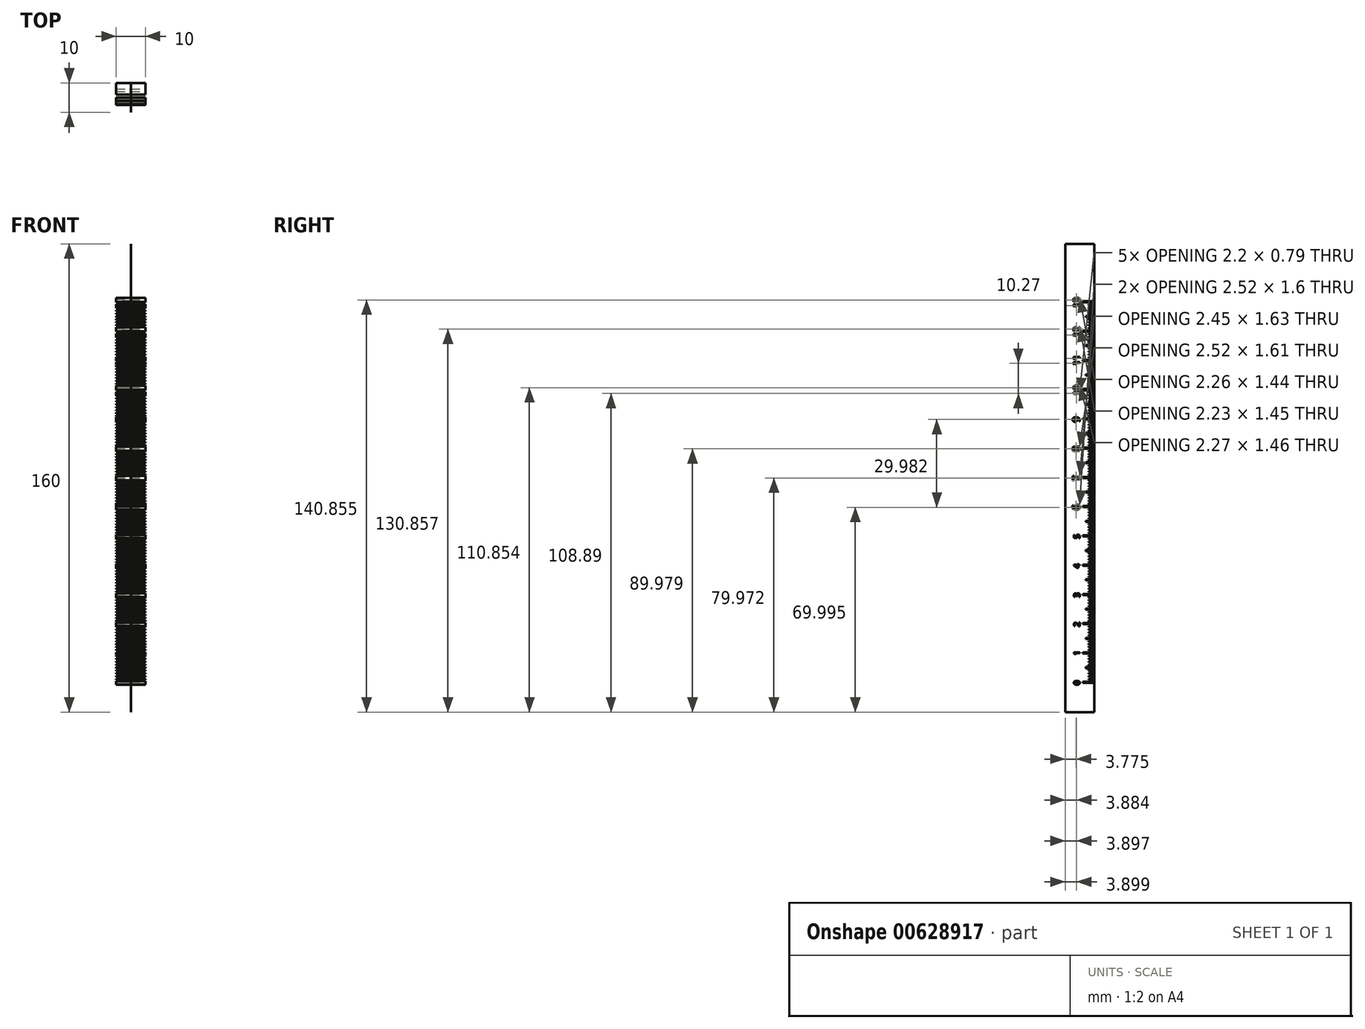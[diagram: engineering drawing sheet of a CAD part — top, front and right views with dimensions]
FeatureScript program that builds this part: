
annotation { "Feature Type Name" : "Feature", "Feature Type Description" : "" }
export const myFeature = defineFeature(function(context is Context, id is Id, definition is map)
    precondition{}
    {
        {
            var Q0;
            Q0=qCreatedBy(makeId("Right.planeOp"),FACE);
            var sketch = newSketch(context, id + "F0", { "sketchPlane" : qUnion([Q0])});
            skLineSegment(sketch, "E0.bottom", {"start": v(-20, 0) * mm, "end": v(-10, 0) * mm});
            skLineSegment(sketch, "E0.top", {"start": v(-20, 160) * mm, "end": v(-10, 160) * mm});
            skLineSegment(sketch, "E0.left", {"start": v(-20, 0) * mm, "end": v(-20, 160) * mm});
            skLineSegment(sketch, "E0.right", {"start": v(-10, 0) * mm, "end": v(-10, 160) * mm});
            skSolve(sketch);
        }
        {
            var Q0;
            Q0=qSketchRegion(id+"F0",true);
            extrude(context, id + "F1", {"entities" : qUnion([Q0]), "depth" : 0.1 * mm, "offsetDistance" : 25 * mm});
        }
        {
            var Q0;
            Q0=qCreatedBy(makeId("Right.planeOp"),FACE);
            var sketch = newSketch(context, id + "F2", { "sketchPlane" : qUnion([Q0])});
            skLineSegment(sketch, "E1", {"start": v(-12, 0) * mm, "end": v(-12, 150) * mm, "construction": true});
            skLineSegment(sketch, "E2", {"start": v(-14, 0) * mm, "end": v(-14, 150) * mm, "construction": true});
            skLineSegment(sketch, "E3", {"start": v(-13, 0) * mm, "end": v(-13, 150) * mm, "construction": true});
            skLineSegment(sketch, "E4.bottom", {"start": v(-14, 10.4) * mm, "end": v(-10, 10.4) * mm});
            skLineSegment(sketch, "E4.top", {"start": v(-14, 10) * mm, "end": v(-10, 10) * mm});
            skLineSegment(sketch, "E4.left", {"start": v(-14, 10) * mm, "end": v(-14, 10.4) * mm});
            skLineSegment(sketch, "E4.right", {"start": v(-10, 10) * mm, "end": v(-10, 10.4) * mm});
            skLineSegment(sketch, "E5.0.1.0", {"start": v(-14, 20.4) * mm, "end": v(-10, 20.4) * mm});
            skLineSegment(sketch, "E5.0.1.1", {"start": v(-14, 20) * mm, "end": v(-10, 20) * mm});
            skLineSegment(sketch, "E5.0.1.2", {"start": v(-14, 20) * mm, "end": v(-14, 20.4) * mm});
            skLineSegment(sketch, "E5.0.1.3", {"start": v(-10, 20) * mm, "end": v(-10, 20.4) * mm});
            skLineSegment(sketch, "E5.0.2.0", {"start": v(-14, 30.4) * mm, "end": v(-10, 30.4) * mm});
            skLineSegment(sketch, "E5.0.2.1", {"start": v(-14, 30) * mm, "end": v(-10, 30) * mm});
            skLineSegment(sketch, "E5.0.2.2", {"start": v(-14, 30) * mm, "end": v(-14, 30.4) * mm});
            skLineSegment(sketch, "E5.0.2.3", {"start": v(-10, 30) * mm, "end": v(-10, 30.4) * mm});
            skLineSegment(sketch, "E5.0.3.0", {"start": v(-14, 40.4) * mm, "end": v(-10, 40.4) * mm});
            skLineSegment(sketch, "E5.0.3.1", {"start": v(-14, 40) * mm, "end": v(-10, 40) * mm});
            skLineSegment(sketch, "E5.0.3.2", {"start": v(-14, 40) * mm, "end": v(-14, 40.4) * mm});
            skLineSegment(sketch, "E5.0.3.3", {"start": v(-10, 40) * mm, "end": v(-10, 40.4) * mm});
            skLineSegment(sketch, "E5.0.4.0", {"start": v(-14, 50.4) * mm, "end": v(-10, 50.4) * mm});
            skLineSegment(sketch, "E5.0.4.1", {"start": v(-14, 50) * mm, "end": v(-10, 50) * mm});
            skLineSegment(sketch, "E5.0.4.2", {"start": v(-14, 50) * mm, "end": v(-14, 50.4) * mm});
            skLineSegment(sketch, "E5.0.4.3", {"start": v(-10, 50) * mm, "end": v(-10, 50.4) * mm});
            skLineSegment(sketch, "E5.0.5.0", {"start": v(-14, 60.4) * mm, "end": v(-10, 60.4) * mm});
            skLineSegment(sketch, "E5.0.5.1", {"start": v(-14, 60) * mm, "end": v(-10, 60) * mm});
            skLineSegment(sketch, "E5.0.5.2", {"start": v(-14, 60) * mm, "end": v(-14, 60.4) * mm});
            skLineSegment(sketch, "E5.0.5.3", {"start": v(-10, 60) * mm, "end": v(-10, 60.4) * mm});
            skLineSegment(sketch, "E5.0.6.0", {"start": v(-14, 70.4) * mm, "end": v(-10, 70.4) * mm});
            skLineSegment(sketch, "E5.0.6.1", {"start": v(-14, 70) * mm, "end": v(-10, 70) * mm});
            skLineSegment(sketch, "E5.0.6.2", {"start": v(-14, 70) * mm, "end": v(-14, 70.4) * mm});
            skLineSegment(sketch, "E5.0.6.3", {"start": v(-10, 70) * mm, "end": v(-10, 70.4) * mm});
            skLineSegment(sketch, "E5.0.7.0", {"start": v(-14, 80.4) * mm, "end": v(-10, 80.4) * mm});
            skLineSegment(sketch, "E5.0.7.1", {"start": v(-14, 80) * mm, "end": v(-10, 80) * mm});
            skLineSegment(sketch, "E5.0.7.2", {"start": v(-14, 80) * mm, "end": v(-14, 80.4) * mm});
            skLineSegment(sketch, "E5.0.7.3", {"start": v(-10, 80) * mm, "end": v(-10, 80.4) * mm});
            skLineSegment(sketch, "E5.0.8.0", {"start": v(-14, 90.4) * mm, "end": v(-10, 90.4) * mm});
            skLineSegment(sketch, "E5.0.8.1", {"start": v(-14, 90) * mm, "end": v(-10, 90) * mm});
            skLineSegment(sketch, "E5.0.8.2", {"start": v(-14, 90) * mm, "end": v(-14, 90.4) * mm});
            skLineSegment(sketch, "E5.0.8.3", {"start": v(-10, 90) * mm, "end": v(-10, 90.4) * mm});
            skLineSegment(sketch, "E5.0.9.0", {"start": v(-14, 100.4) * mm, "end": v(-10, 100.4) * mm});
            skLineSegment(sketch, "E5.0.9.1", {"start": v(-14, 100) * mm, "end": v(-10, 100) * mm});
            skLineSegment(sketch, "E5.0.9.2", {"start": v(-14, 100) * mm, "end": v(-14, 100.4) * mm});
            skLineSegment(sketch, "E5.0.9.3", {"start": v(-10, 100) * mm, "end": v(-10, 100.4) * mm});
            skLineSegment(sketch, "E5.direction2", {"start": v(-14, 10) * mm, "end": v(-14, 20) * mm, "construction": true});
            skLineSegment(sketch, "E6.0.0.10", {"start": v(-14, 110.4) * mm, "end": v(-10, 110.4) * mm});
            skLineSegment(sketch, "E6.3.0.10", {"start": v(-14, 110) * mm, "end": v(-10, 110) * mm});
            skLineSegment(sketch, "E6.6.0.10", {"start": v(-14, 110) * mm, "end": v(-14, 110.4) * mm});
            skLineSegment(sketch, "E6.9.0.10", {"start": v(-10, 110) * mm, "end": v(-10, 110.4) * mm});
            skLineSegment(sketch, "E6.0.0.11", {"start": v(-14, 120.4) * mm, "end": v(-10, 120.4) * mm});
            skLineSegment(sketch, "E6.3.0.11", {"start": v(-14, 120) * mm, "end": v(-10, 120) * mm});
            skLineSegment(sketch, "E6.6.0.11", {"start": v(-14, 120) * mm, "end": v(-14, 120.4) * mm});
            skLineSegment(sketch, "E6.9.0.11", {"start": v(-10, 120) * mm, "end": v(-10, 120.4) * mm});
            skLineSegment(sketch, "E6.0.0.12", {"start": v(-14, 130.4) * mm, "end": v(-10, 130.4) * mm});
            skLineSegment(sketch, "E6.3.0.12", {"start": v(-14, 130) * mm, "end": v(-10, 130) * mm});
            skLineSegment(sketch, "E6.6.0.12", {"start": v(-14, 130) * mm, "end": v(-14, 130.4) * mm});
            skLineSegment(sketch, "E6.9.0.12", {"start": v(-10, 130) * mm, "end": v(-10, 130.4) * mm});
            skLineSegment(sketch, "E6.0.0.13", {"start": v(-14, 140.4) * mm, "end": v(-10, 140.4) * mm});
            skLineSegment(sketch, "E6.3.0.13", {"start": v(-14, 140) * mm, "end": v(-10, 140) * mm});
            skLineSegment(sketch, "E6.6.0.13", {"start": v(-14, 140) * mm, "end": v(-14, 140.4) * mm});
            skLineSegment(sketch, "E6.9.0.13", {"start": v(-10, 140) * mm, "end": v(-10, 140.4) * mm});
            skLineSegment(sketch, "E7.bottom", {"start": v(-10, 15) * mm, "end": v(-13, 15) * mm});
            skLineSegment(sketch, "E7.top", {"start": v(-10, 15.4) * mm, "end": v(-13, 15.4) * mm});
            skLineSegment(sketch, "E7.left", {"start": v(-10, 15) * mm, "end": v(-10, 15.4) * mm});
            skLineSegment(sketch, "E7.right", {"start": v(-13, 15) * mm, "end": v(-13, 15.4) * mm});
            skLineSegment(sketch, "E8", {"start": v(-22.56, 0) * mm, "end": v(-10, 0) * mm, "construction": true});
            skLineSegment(sketch, "E9", {"start": v(-15, 150) * mm, "end": v(-15, 0) * mm, "construction": true});
            skText(sketch, "E10", { "text": "0", "fontName": "OpenSans-Regular.ttf"});
            skText(sketch, "E11", { "text": "1\n", "fontName": "OpenSans-Regular.ttf"});
            skText(sketch, "E12", { "text": "2", "fontName": "OpenSans-Regular.ttf"});
            skText(sketch, "E13", { "text": "3", "fontName": "OpenSans-Regular.ttf"});
            skText(sketch, "E14", { "text": "4", "fontName": "OpenSans-Regular.ttf"});
            skText(sketch, "E15", { "text": "5", "fontName": "OpenSans-Regular.ttf"});
            skText(sketch, "E16", { "text": "6", "fontName": "OpenSans-Regular.ttf"});
            skText(sketch, "E17", { "text": "7", "fontName": "OpenSans-Regular.ttf"});
            skText(sketch, "E18", { "text": "8", "fontName": "OpenSans-Regular.ttf"});
            skText(sketch, "E19", { "text": "9", "fontName": "OpenSans-Regular.ttf"});
            skText(sketch, "E20", { "text": "10", "fontName": "OpenSans-Regular.ttf"});
            skText(sketch, "E21", { "text": "11", "fontName": "OpenSans-Regular.ttf"});
            skText(sketch, "E22", { "text": "12", "fontName": "OpenSans-Regular.ttf"});
            skText(sketch, "E23", { "text": "13", "fontName": "OpenSans-Regular.ttf"});
            skLineSegment(sketch, "E24.bottom", {"start": v(-12, 11) * mm, "end": v(-10, 11) * mm});
            skLineSegment(sketch, "E24.top", {"start": v(-12, 11.4) * mm, "end": v(-10, 11.4) * mm});
            skLineSegment(sketch, "E24.left", {"start": v(-12, 11) * mm, "end": v(-12, 11.4) * mm});
            skLineSegment(sketch, "E24.right", {"start": v(-10, 11) * mm, "end": v(-10, 11.4) * mm});
            skLineSegment(sketch, "E25.bottom", {"start": v(-12, 12) * mm, "end": v(-10, 12) * mm});
            skLineSegment(sketch, "E25.top", {"start": v(-12, 12.4) * mm, "end": v(-10, 12.4) * mm});
            skLineSegment(sketch, "E25.left", {"start": v(-12, 12) * mm, "end": v(-12, 12.4) * mm});
            skLineSegment(sketch, "E25.right", {"start": v(-10, 12) * mm, "end": v(-10, 12.4) * mm});
            skLineSegment(sketch, "E26.bottom", {"start": v(-12, 13) * mm, "end": v(-10, 13) * mm});
            skLineSegment(sketch, "E26.top", {"start": v(-12, 13.4) * mm, "end": v(-10, 13.4) * mm});
            skLineSegment(sketch, "E26.left", {"start": v(-12, 13) * mm, "end": v(-12, 13.4) * mm});
            skLineSegment(sketch, "E26.right", {"start": v(-10, 13) * mm, "end": v(-10, 13.4) * mm});
            skLineSegment(sketch, "E27.bottom", {"start": v(-12, 14) * mm, "end": v(-10, 14) * mm});
            skLineSegment(sketch, "E27.top", {"start": v(-12, 14.4) * mm, "end": v(-10, 14.4) * mm});
            skLineSegment(sketch, "E27.left", {"start": v(-12, 14) * mm, "end": v(-12, 14.4) * mm});
            skLineSegment(sketch, "E27.right", {"start": v(-10, 14) * mm, "end": v(-10, 14.4) * mm});
            skLineSegment(sketch, "E28.bottom", {"start": v(-12, 16) * mm, "end": v(-10, 16) * mm});
            skLineSegment(sketch, "E28.top", {"start": v(-12, 16.4) * mm, "end": v(-10, 16.4) * mm});
            skLineSegment(sketch, "E28.left", {"start": v(-12, 16) * mm, "end": v(-12, 16.4) * mm});
            skLineSegment(sketch, "E28.right", {"start": v(-10, 16) * mm, "end": v(-10, 16.4) * mm});
            skLineSegment(sketch, "E29.bottom", {"start": v(-12, 17) * mm, "end": v(-10, 17) * mm});
            skLineSegment(sketch, "E29.top", {"start": v(-12, 17.4) * mm, "end": v(-10, 17.4) * mm});
            skLineSegment(sketch, "E29.left", {"start": v(-12, 17) * mm, "end": v(-12, 17.4) * mm});
            skLineSegment(sketch, "E29.right", {"start": v(-10, 17) * mm, "end": v(-10, 17.4) * mm});
            skLineSegment(sketch, "E30.bottom", {"start": v(-12, 18) * mm, "end": v(-10, 18) * mm});
            skLineSegment(sketch, "E30.top", {"start": v(-12, 18.4) * mm, "end": v(-10, 18.4) * mm});
            skLineSegment(sketch, "E30.left", {"start": v(-12, 18) * mm, "end": v(-12, 18.4) * mm});
            skLineSegment(sketch, "E30.right", {"start": v(-10, 18) * mm, "end": v(-10, 18.4) * mm});
            skLineSegment(sketch, "E31.bottom", {"start": v(-12, 19) * mm, "end": v(-10, 19) * mm});
            skLineSegment(sketch, "E31.top", {"start": v(-12, 19.4) * mm, "end": v(-10, 19.4) * mm});
            skLineSegment(sketch, "E31.left", {"start": v(-12, 19) * mm, "end": v(-12, 19.4) * mm});
            skLineSegment(sketch, "E31.right", {"start": v(-10, 19) * mm, "end": v(-10, 19.4) * mm});
            skLineSegment(sketch, "E32.0.1.0", {"start": v(-12, 22) * mm, "end": v(-10, 22) * mm});
            skLineSegment(sketch, "E32.0.1.1", {"start": v(-12, 21.4) * mm, "end": v(-10, 21.4) * mm});
            skLineSegment(sketch, "E32.0.1.2", {"start": v(-12, 23.4) * mm, "end": v(-10, 23.4) * mm});
            skLineSegment(sketch, "E32.0.1.3", {"start": v(-12, 28.4) * mm, "end": v(-10, 28.4) * mm});
            skLineSegment(sketch, "E32.0.1.4", {"start": v(-12, 22.4) * mm, "end": v(-10, 22.4) * mm});
            skLineSegment(sketch, "E32.0.1.5", {"start": v(-12, 23) * mm, "end": v(-10, 23) * mm});
            skLineSegment(sketch, "E32.0.1.6", {"start": v(-10, 25.4) * mm, "end": v(-13, 25.4) * mm});
            skLineSegment(sketch, "E32.0.1.7", {"start": v(-12, 29) * mm, "end": v(-10, 29) * mm});
            skLineSegment(sketch, "E32.0.1.8", {"start": v(-12, 29.4) * mm, "end": v(-10, 29.4) * mm});
            skLineSegment(sketch, "E32.0.1.9", {"start": v(-12, 24.4) * mm, "end": v(-10, 24.4) * mm});
            skLineSegment(sketch, "E32.0.1.10", {"start": v(-12, 28) * mm, "end": v(-10, 28) * mm});
            skLineSegment(sketch, "E32.0.1.11", {"start": v(-12, 26) * mm, "end": v(-10, 26) * mm});
            skLineSegment(sketch, "E32.0.1.12", {"start": v(-12, 27) * mm, "end": v(-10, 27) * mm});
            skLineSegment(sketch, "E32.0.1.13", {"start": v(-12, 26.4) * mm, "end": v(-10, 26.4) * mm});
            skLineSegment(sketch, "E32.0.1.14", {"start": v(-12, 21) * mm, "end": v(-10, 21) * mm});
            skLineSegment(sketch, "E32.0.1.15", {"start": v(-10, 25) * mm, "end": v(-13, 25) * mm});
            skLineSegment(sketch, "E32.0.1.16", {"start": v(-12, 10) * mm, "end": v(-12, 160) * mm, "construction": true});
            skLineSegment(sketch, "E32.0.1.17", {"start": v(-13, 10) * mm, "end": v(-13, 160) * mm, "construction": true});
            skLineSegment(sketch, "E32.0.1.18", {"start": v(-12, 24) * mm, "end": v(-10, 24) * mm});
            skLineSegment(sketch, "E32.0.1.19", {"start": v(-12, 27.4) * mm, "end": v(-10, 27.4) * mm});
            skLineSegment(sketch, "E32.0.1.20", {"start": v(-12, 21) * mm, "end": v(-12, 21.4) * mm});
            skLineSegment(sketch, "E32.0.1.21", {"start": v(-10, 24) * mm, "end": v(-10, 24.4) * mm});
            skLineSegment(sketch, "E32.0.1.22", {"start": v(-10, 27) * mm, "end": v(-10, 27.4) * mm});
            skLineSegment(sketch, "E32.0.1.23", {"start": v(-12, 29) * mm, "end": v(-12, 29.4) * mm});
            skLineSegment(sketch, "E32.0.1.24", {"start": v(-10, 25) * mm, "end": v(-10, 25.4) * mm});
            skLineSegment(sketch, "E32.0.1.25", {"start": v(-12, 24) * mm, "end": v(-12, 24.4) * mm});
            skLineSegment(sketch, "E32.0.1.26", {"start": v(-12, 26) * mm, "end": v(-12, 26.4) * mm});
            skLineSegment(sketch, "E32.0.1.27", {"start": v(-10, 28) * mm, "end": v(-10, 28.4) * mm});
            skLineSegment(sketch, "E32.0.1.28", {"start": v(-12, 28) * mm, "end": v(-12, 28.4) * mm});
            skLineSegment(sketch, "E32.0.1.29", {"start": v(-10, 21) * mm, "end": v(-10, 21.4) * mm});
            skLineSegment(sketch, "E32.0.1.30", {"start": v(-10, 26) * mm, "end": v(-10, 26.4) * mm});
            skLineSegment(sketch, "E32.0.1.31", {"start": v(-10, 29) * mm, "end": v(-10, 29.4) * mm});
            skLineSegment(sketch, "E32.0.1.32", {"start": v(-12, 22) * mm, "end": v(-12, 22.4) * mm});
            skLineSegment(sketch, "E32.0.1.33", {"start": v(-10, 23) * mm, "end": v(-10, 23.4) * mm});
            skLineSegment(sketch, "E32.0.1.34", {"start": v(-13, 25) * mm, "end": v(-13, 25.4) * mm});
            skLineSegment(sketch, "E32.0.1.35", {"start": v(-10, 22) * mm, "end": v(-10, 22.4) * mm});
            skLineSegment(sketch, "E32.0.1.36", {"start": v(-12, 27) * mm, "end": v(-12, 27.4) * mm});
            skLineSegment(sketch, "E32.0.1.37", {"start": v(-12, 23) * mm, "end": v(-12, 23.4) * mm});
            skLineSegment(sketch, "E32.0.2.0", {"start": v(-12, 32) * mm, "end": v(-10, 32) * mm});
            skLineSegment(sketch, "E32.0.2.1", {"start": v(-12, 31.4) * mm, "end": v(-10, 31.4) * mm});
            skLineSegment(sketch, "E32.0.2.2", {"start": v(-12, 33.4) * mm, "end": v(-10, 33.4) * mm});
            skLineSegment(sketch, "E32.0.2.3", {"start": v(-12, 38.4) * mm, "end": v(-10, 38.4) * mm});
            skLineSegment(sketch, "E32.0.2.4", {"start": v(-12, 32.4) * mm, "end": v(-10, 32.4) * mm});
            skLineSegment(sketch, "E32.0.2.5", {"start": v(-12, 33) * mm, "end": v(-10, 33) * mm});
            skLineSegment(sketch, "E32.0.2.6", {"start": v(-10, 35.4) * mm, "end": v(-13, 35.4) * mm});
            skLineSegment(sketch, "E32.0.2.7", {"start": v(-12, 39) * mm, "end": v(-10, 39) * mm});
            skLineSegment(sketch, "E32.0.2.8", {"start": v(-12, 39.4) * mm, "end": v(-10, 39.4) * mm});
            skLineSegment(sketch, "E32.0.2.9", {"start": v(-12, 34.4) * mm, "end": v(-10, 34.4) * mm});
            skLineSegment(sketch, "E32.0.2.10", {"start": v(-12, 38) * mm, "end": v(-10, 38) * mm});
            skLineSegment(sketch, "E32.0.2.11", {"start": v(-12, 36) * mm, "end": v(-10, 36) * mm});
            skLineSegment(sketch, "E32.0.2.12", {"start": v(-12, 37) * mm, "end": v(-10, 37) * mm});
            skLineSegment(sketch, "E32.0.2.13", {"start": v(-12, 36.4) * mm, "end": v(-10, 36.4) * mm});
            skLineSegment(sketch, "E32.0.2.14", {"start": v(-12, 31) * mm, "end": v(-10, 31) * mm});
            skLineSegment(sketch, "E32.0.2.15", {"start": v(-10, 35) * mm, "end": v(-13, 35) * mm});
            skLineSegment(sketch, "E32.0.2.16", {"start": v(-12, 20) * mm, "end": v(-12, 170) * mm, "construction": true});
            skLineSegment(sketch, "E32.0.2.17", {"start": v(-13, 20) * mm, "end": v(-13, 170) * mm, "construction": true});
            skLineSegment(sketch, "E32.0.2.18", {"start": v(-12, 34) * mm, "end": v(-10, 34) * mm});
            skLineSegment(sketch, "E32.0.2.19", {"start": v(-12, 37.4) * mm, "end": v(-10, 37.4) * mm});
            skLineSegment(sketch, "E32.0.2.20", {"start": v(-12, 31) * mm, "end": v(-12, 31.4) * mm});
            skLineSegment(sketch, "E32.0.2.21", {"start": v(-10, 34) * mm, "end": v(-10, 34.4) * mm});
            skLineSegment(sketch, "E32.0.2.22", {"start": v(-10, 37) * mm, "end": v(-10, 37.4) * mm});
            skLineSegment(sketch, "E32.0.2.23", {"start": v(-12, 39) * mm, "end": v(-12, 39.4) * mm});
            skLineSegment(sketch, "E32.0.2.24", {"start": v(-10, 35) * mm, "end": v(-10, 35.4) * mm});
            skLineSegment(sketch, "E32.0.2.25", {"start": v(-12, 34) * mm, "end": v(-12, 34.4) * mm});
            skLineSegment(sketch, "E32.0.2.26", {"start": v(-12, 36) * mm, "end": v(-12, 36.4) * mm});
            skLineSegment(sketch, "E32.0.2.27", {"start": v(-10, 38) * mm, "end": v(-10, 38.4) * mm});
            skLineSegment(sketch, "E32.0.2.28", {"start": v(-12, 38) * mm, "end": v(-12, 38.4) * mm});
            skLineSegment(sketch, "E32.0.2.29", {"start": v(-10, 31) * mm, "end": v(-10, 31.4) * mm});
            skLineSegment(sketch, "E32.0.2.30", {"start": v(-10, 36) * mm, "end": v(-10, 36.4) * mm});
            skLineSegment(sketch, "E32.0.2.31", {"start": v(-10, 39) * mm, "end": v(-10, 39.4) * mm});
            skLineSegment(sketch, "E32.0.2.32", {"start": v(-12, 32) * mm, "end": v(-12, 32.4) * mm});
            skLineSegment(sketch, "E32.0.2.33", {"start": v(-10, 33) * mm, "end": v(-10, 33.4) * mm});
            skLineSegment(sketch, "E32.0.2.34", {"start": v(-13, 35) * mm, "end": v(-13, 35.4) * mm});
            skLineSegment(sketch, "E32.0.2.35", {"start": v(-10, 32) * mm, "end": v(-10, 32.4) * mm});
            skLineSegment(sketch, "E32.0.2.36", {"start": v(-12, 37) * mm, "end": v(-12, 37.4) * mm});
            skLineSegment(sketch, "E32.0.2.37", {"start": v(-12, 33) * mm, "end": v(-12, 33.4) * mm});
            skLineSegment(sketch, "E32.0.3.0", {"start": v(-12, 42) * mm, "end": v(-10, 42) * mm});
            skLineSegment(sketch, "E32.0.3.1", {"start": v(-12, 41.4) * mm, "end": v(-10, 41.4) * mm});
            skLineSegment(sketch, "E32.0.3.2", {"start": v(-12, 43.4) * mm, "end": v(-10, 43.4) * mm});
            skLineSegment(sketch, "E32.0.3.3", {"start": v(-12, 48.4) * mm, "end": v(-10, 48.4) * mm});
            skLineSegment(sketch, "E32.0.3.4", {"start": v(-12, 42.4) * mm, "end": v(-10, 42.4) * mm});
            skLineSegment(sketch, "E32.0.3.5", {"start": v(-12, 43) * mm, "end": v(-10, 43) * mm});
            skLineSegment(sketch, "E32.0.3.6", {"start": v(-10, 45.4) * mm, "end": v(-13, 45.4) * mm});
            skLineSegment(sketch, "E32.0.3.7", {"start": v(-12, 49) * mm, "end": v(-10, 49) * mm});
            skLineSegment(sketch, "E32.0.3.8", {"start": v(-12, 49.4) * mm, "end": v(-10, 49.4) * mm});
            skLineSegment(sketch, "E32.0.3.9", {"start": v(-12, 44.4) * mm, "end": v(-10, 44.4) * mm});
            skLineSegment(sketch, "E32.0.3.10", {"start": v(-12, 48) * mm, "end": v(-10, 48) * mm});
            skLineSegment(sketch, "E32.0.3.11", {"start": v(-12, 46) * mm, "end": v(-10, 46) * mm});
            skLineSegment(sketch, "E32.0.3.12", {"start": v(-12, 47) * mm, "end": v(-10, 47) * mm});
            skLineSegment(sketch, "E32.0.3.13", {"start": v(-12, 46.4) * mm, "end": v(-10, 46.4) * mm});
            skLineSegment(sketch, "E32.0.3.14", {"start": v(-12, 41) * mm, "end": v(-10, 41) * mm});
            skLineSegment(sketch, "E32.0.3.15", {"start": v(-10, 45) * mm, "end": v(-13, 45) * mm});
            skLineSegment(sketch, "E32.0.3.16", {"start": v(-12, 30) * mm, "end": v(-12, 180) * mm, "construction": true});
            skLineSegment(sketch, "E32.0.3.17", {"start": v(-13, 30) * mm, "end": v(-13, 180) * mm, "construction": true});
            skLineSegment(sketch, "E32.0.3.18", {"start": v(-12, 44) * mm, "end": v(-10, 44) * mm});
            skLineSegment(sketch, "E32.0.3.19", {"start": v(-12, 47.4) * mm, "end": v(-10, 47.4) * mm});
            skLineSegment(sketch, "E32.0.3.20", {"start": v(-12, 41) * mm, "end": v(-12, 41.4) * mm});
            skLineSegment(sketch, "E32.0.3.21", {"start": v(-10, 44) * mm, "end": v(-10, 44.4) * mm});
            skLineSegment(sketch, "E32.0.3.22", {"start": v(-10, 47) * mm, "end": v(-10, 47.4) * mm});
            skLineSegment(sketch, "E32.0.3.23", {"start": v(-12, 49) * mm, "end": v(-12, 49.4) * mm});
            skLineSegment(sketch, "E32.0.3.24", {"start": v(-10, 45) * mm, "end": v(-10, 45.4) * mm});
            skLineSegment(sketch, "E32.0.3.25", {"start": v(-12, 44) * mm, "end": v(-12, 44.4) * mm});
            skLineSegment(sketch, "E32.0.3.26", {"start": v(-12, 46) * mm, "end": v(-12, 46.4) * mm});
            skLineSegment(sketch, "E32.0.3.27", {"start": v(-10, 48) * mm, "end": v(-10, 48.4) * mm});
            skLineSegment(sketch, "E32.0.3.28", {"start": v(-12, 48) * mm, "end": v(-12, 48.4) * mm});
            skLineSegment(sketch, "E32.0.3.29", {"start": v(-10, 41) * mm, "end": v(-10, 41.4) * mm});
            skLineSegment(sketch, "E32.0.3.30", {"start": v(-10, 46) * mm, "end": v(-10, 46.4) * mm});
            skLineSegment(sketch, "E32.0.3.31", {"start": v(-10, 49) * mm, "end": v(-10, 49.4) * mm});
            skLineSegment(sketch, "E32.0.3.32", {"start": v(-12, 42) * mm, "end": v(-12, 42.4) * mm});
            skLineSegment(sketch, "E32.0.3.33", {"start": v(-10, 43) * mm, "end": v(-10, 43.4) * mm});
            skLineSegment(sketch, "E32.0.3.34", {"start": v(-13, 45) * mm, "end": v(-13, 45.4) * mm});
            skLineSegment(sketch, "E32.0.3.35", {"start": v(-10, 42) * mm, "end": v(-10, 42.4) * mm});
            skLineSegment(sketch, "E32.0.3.36", {"start": v(-12, 47) * mm, "end": v(-12, 47.4) * mm});
            skLineSegment(sketch, "E32.0.3.37", {"start": v(-12, 43) * mm, "end": v(-12, 43.4) * mm});
            skLineSegment(sketch, "E32.0.4.0", {"start": v(-12, 52) * mm, "end": v(-10, 52) * mm});
            skLineSegment(sketch, "E32.0.4.1", {"start": v(-12, 51.4) * mm, "end": v(-10, 51.4) * mm});
            skLineSegment(sketch, "E32.0.4.2", {"start": v(-12, 53.4) * mm, "end": v(-10, 53.4) * mm});
            skLineSegment(sketch, "E32.0.4.3", {"start": v(-12, 58.4) * mm, "end": v(-10, 58.4) * mm});
            skLineSegment(sketch, "E32.0.4.4", {"start": v(-12, 52.4) * mm, "end": v(-10, 52.4) * mm});
            skLineSegment(sketch, "E32.0.4.5", {"start": v(-12, 53) * mm, "end": v(-10, 53) * mm});
            skLineSegment(sketch, "E32.0.4.6", {"start": v(-10, 55.4) * mm, "end": v(-13, 55.4) * mm});
            skLineSegment(sketch, "E32.0.4.7", {"start": v(-12, 59) * mm, "end": v(-10, 59) * mm});
            skLineSegment(sketch, "E32.0.4.8", {"start": v(-12, 59.4) * mm, "end": v(-10, 59.4) * mm});
            skLineSegment(sketch, "E32.0.4.9", {"start": v(-12, 54.4) * mm, "end": v(-10, 54.4) * mm});
            skLineSegment(sketch, "E32.0.4.10", {"start": v(-12, 58) * mm, "end": v(-10, 58) * mm});
            skLineSegment(sketch, "E32.0.4.11", {"start": v(-12, 56) * mm, "end": v(-10, 56) * mm});
            skLineSegment(sketch, "E32.0.4.12", {"start": v(-12, 57) * mm, "end": v(-10, 57) * mm});
            skLineSegment(sketch, "E32.0.4.13", {"start": v(-12, 56.4) * mm, "end": v(-10, 56.4) * mm});
            skLineSegment(sketch, "E32.0.4.14", {"start": v(-12, 51) * mm, "end": v(-10, 51) * mm});
            skLineSegment(sketch, "E32.0.4.15", {"start": v(-10, 55) * mm, "end": v(-13, 55) * mm});
            skLineSegment(sketch, "E32.0.4.16", {"start": v(-12, 40) * mm, "end": v(-12, 190) * mm, "construction": true});
            skLineSegment(sketch, "E32.0.4.17", {"start": v(-13, 40) * mm, "end": v(-13, 190) * mm, "construction": true});
            skLineSegment(sketch, "E32.0.4.18", {"start": v(-12, 54) * mm, "end": v(-10, 54) * mm});
            skLineSegment(sketch, "E32.0.4.19", {"start": v(-12, 57.4) * mm, "end": v(-10, 57.4) * mm});
            skLineSegment(sketch, "E32.0.4.20", {"start": v(-12, 51) * mm, "end": v(-12, 51.4) * mm});
            skLineSegment(sketch, "E32.0.4.21", {"start": v(-10, 54) * mm, "end": v(-10, 54.4) * mm});
            skLineSegment(sketch, "E32.0.4.22", {"start": v(-10, 57) * mm, "end": v(-10, 57.4) * mm});
            skLineSegment(sketch, "E32.0.4.23", {"start": v(-12, 59) * mm, "end": v(-12, 59.4) * mm});
            skLineSegment(sketch, "E32.0.4.24", {"start": v(-10, 55) * mm, "end": v(-10, 55.4) * mm});
            skLineSegment(sketch, "E32.0.4.25", {"start": v(-12, 54) * mm, "end": v(-12, 54.4) * mm});
            skLineSegment(sketch, "E32.0.4.26", {"start": v(-12, 56) * mm, "end": v(-12, 56.4) * mm});
            skLineSegment(sketch, "E32.0.4.27", {"start": v(-10, 58) * mm, "end": v(-10, 58.4) * mm});
            skLineSegment(sketch, "E32.0.4.28", {"start": v(-12, 58) * mm, "end": v(-12, 58.4) * mm});
            skLineSegment(sketch, "E32.0.4.29", {"start": v(-10, 51) * mm, "end": v(-10, 51.4) * mm});
            skLineSegment(sketch, "E32.0.4.30", {"start": v(-10, 56) * mm, "end": v(-10, 56.4) * mm});
            skLineSegment(sketch, "E32.0.4.31", {"start": v(-10, 59) * mm, "end": v(-10, 59.4) * mm});
            skLineSegment(sketch, "E32.0.4.32", {"start": v(-12, 52) * mm, "end": v(-12, 52.4) * mm});
            skLineSegment(sketch, "E32.0.4.33", {"start": v(-10, 53) * mm, "end": v(-10, 53.4) * mm});
            skLineSegment(sketch, "E32.0.4.34", {"start": v(-13, 55) * mm, "end": v(-13, 55.4) * mm});
            skLineSegment(sketch, "E32.0.4.35", {"start": v(-10, 52) * mm, "end": v(-10, 52.4) * mm});
            skLineSegment(sketch, "E32.0.4.36", {"start": v(-12, 57) * mm, "end": v(-12, 57.4) * mm});
            skLineSegment(sketch, "E32.0.4.37", {"start": v(-12, 53) * mm, "end": v(-12, 53.4) * mm});
            skLineSegment(sketch, "E32.0.5.0", {"start": v(-12, 62) * mm, "end": v(-10, 62) * mm});
            skLineSegment(sketch, "E32.0.5.1", {"start": v(-12, 61.4) * mm, "end": v(-10, 61.4) * mm});
            skLineSegment(sketch, "E32.0.5.2", {"start": v(-12, 63.4) * mm, "end": v(-10, 63.4) * mm});
            skLineSegment(sketch, "E32.0.5.3", {"start": v(-12, 68.4) * mm, "end": v(-10, 68.4) * mm});
            skLineSegment(sketch, "E32.0.5.4", {"start": v(-12, 62.4) * mm, "end": v(-10, 62.4) * mm});
            skLineSegment(sketch, "E32.0.5.5", {"start": v(-12, 63) * mm, "end": v(-10, 63) * mm});
            skLineSegment(sketch, "E32.0.5.6", {"start": v(-10, 65.4) * mm, "end": v(-13, 65.4) * mm});
            skLineSegment(sketch, "E32.0.5.7", {"start": v(-12, 69) * mm, "end": v(-10, 69) * mm});
            skLineSegment(sketch, "E32.0.5.8", {"start": v(-12, 69.4) * mm, "end": v(-10, 69.4) * mm});
            skLineSegment(sketch, "E32.0.5.9", {"start": v(-12, 64.4) * mm, "end": v(-10, 64.4) * mm});
            skLineSegment(sketch, "E32.0.5.10", {"start": v(-12, 68) * mm, "end": v(-10, 68) * mm});
            skLineSegment(sketch, "E32.0.5.11", {"start": v(-12, 66) * mm, "end": v(-10, 66) * mm});
            skLineSegment(sketch, "E32.0.5.12", {"start": v(-12, 67) * mm, "end": v(-10, 67) * mm});
            skLineSegment(sketch, "E32.0.5.13", {"start": v(-12, 66.4) * mm, "end": v(-10, 66.4) * mm});
            skLineSegment(sketch, "E32.0.5.14", {"start": v(-12, 61) * mm, "end": v(-10, 61) * mm});
            skLineSegment(sketch, "E32.0.5.15", {"start": v(-10, 65) * mm, "end": v(-13, 65) * mm});
            skLineSegment(sketch, "E32.0.5.16", {"start": v(-12, 50) * mm, "end": v(-12, 200) * mm, "construction": true});
            skLineSegment(sketch, "E32.0.5.17", {"start": v(-13, 50) * mm, "end": v(-13, 200) * mm, "construction": true});
            skLineSegment(sketch, "E32.0.5.18", {"start": v(-12, 64) * mm, "end": v(-10, 64) * mm});
            skLineSegment(sketch, "E32.0.5.19", {"start": v(-12, 67.4) * mm, "end": v(-10, 67.4) * mm});
            skLineSegment(sketch, "E32.0.5.20", {"start": v(-12, 61) * mm, "end": v(-12, 61.4) * mm});
            skLineSegment(sketch, "E32.0.5.21", {"start": v(-10, 64) * mm, "end": v(-10, 64.4) * mm});
            skLineSegment(sketch, "E32.0.5.22", {"start": v(-10, 67) * mm, "end": v(-10, 67.4) * mm});
            skLineSegment(sketch, "E32.0.5.23", {"start": v(-12, 69) * mm, "end": v(-12, 69.4) * mm});
            skLineSegment(sketch, "E32.0.5.24", {"start": v(-10, 65) * mm, "end": v(-10, 65.4) * mm});
            skLineSegment(sketch, "E32.0.5.25", {"start": v(-12, 64) * mm, "end": v(-12, 64.4) * mm});
            skLineSegment(sketch, "E32.0.5.26", {"start": v(-12, 66) * mm, "end": v(-12, 66.4) * mm});
            skLineSegment(sketch, "E32.0.5.27", {"start": v(-10, 68) * mm, "end": v(-10, 68.4) * mm});
            skLineSegment(sketch, "E32.0.5.28", {"start": v(-12, 68) * mm, "end": v(-12, 68.4) * mm});
            skLineSegment(sketch, "E32.0.5.29", {"start": v(-10, 61) * mm, "end": v(-10, 61.4) * mm});
            skLineSegment(sketch, "E32.0.5.30", {"start": v(-10, 66) * mm, "end": v(-10, 66.4) * mm});
            skLineSegment(sketch, "E32.0.5.31", {"start": v(-10, 69) * mm, "end": v(-10, 69.4) * mm});
            skLineSegment(sketch, "E32.0.5.32", {"start": v(-12, 62) * mm, "end": v(-12, 62.4) * mm});
            skLineSegment(sketch, "E32.0.5.33", {"start": v(-10, 63) * mm, "end": v(-10, 63.4) * mm});
            skLineSegment(sketch, "E32.0.5.34", {"start": v(-13, 65) * mm, "end": v(-13, 65.4) * mm});
            skLineSegment(sketch, "E32.0.5.35", {"start": v(-10, 62) * mm, "end": v(-10, 62.4) * mm});
            skLineSegment(sketch, "E32.0.5.36", {"start": v(-12, 67) * mm, "end": v(-12, 67.4) * mm});
            skLineSegment(sketch, "E32.0.5.37", {"start": v(-12, 63) * mm, "end": v(-12, 63.4) * mm});
            skLineSegment(sketch, "E32.0.6.0", {"start": v(-12, 72) * mm, "end": v(-10, 72) * mm});
            skLineSegment(sketch, "E32.0.6.1", {"start": v(-12, 71.4) * mm, "end": v(-10, 71.4) * mm});
            skLineSegment(sketch, "E32.0.6.2", {"start": v(-12, 73.4) * mm, "end": v(-10, 73.4) * mm});
            skLineSegment(sketch, "E32.0.6.3", {"start": v(-12, 78.4) * mm, "end": v(-10, 78.4) * mm});
            skLineSegment(sketch, "E32.0.6.4", {"start": v(-12, 72.4) * mm, "end": v(-10, 72.4) * mm});
            skLineSegment(sketch, "E32.0.6.5", {"start": v(-12, 73) * mm, "end": v(-10, 73) * mm});
            skLineSegment(sketch, "E32.0.6.6", {"start": v(-10, 75.4) * mm, "end": v(-13, 75.4) * mm});
            skLineSegment(sketch, "E32.0.6.7", {"start": v(-12, 79) * mm, "end": v(-10, 79) * mm});
            skLineSegment(sketch, "E32.0.6.8", {"start": v(-12, 79.4) * mm, "end": v(-10, 79.4) * mm});
            skLineSegment(sketch, "E32.0.6.9", {"start": v(-12, 74.4) * mm, "end": v(-10, 74.4) * mm});
            skLineSegment(sketch, "E32.0.6.10", {"start": v(-12, 78) * mm, "end": v(-10, 78) * mm});
            skLineSegment(sketch, "E32.0.6.11", {"start": v(-12, 76) * mm, "end": v(-10, 76) * mm});
            skLineSegment(sketch, "E32.0.6.12", {"start": v(-12, 77) * mm, "end": v(-10, 77) * mm});
            skLineSegment(sketch, "E32.0.6.13", {"start": v(-12, 76.4) * mm, "end": v(-10, 76.4) * mm});
            skLineSegment(sketch, "E32.0.6.14", {"start": v(-12, 71) * mm, "end": v(-10, 71) * mm});
            skLineSegment(sketch, "E32.0.6.15", {"start": v(-10, 75) * mm, "end": v(-13, 75) * mm});
            skLineSegment(sketch, "E32.0.6.16", {"start": v(-12, 60) * mm, "end": v(-12, 210) * mm, "construction": true});
            skLineSegment(sketch, "E32.0.6.17", {"start": v(-13, 60) * mm, "end": v(-13, 210) * mm, "construction": true});
            skLineSegment(sketch, "E32.0.6.18", {"start": v(-12, 74) * mm, "end": v(-10, 74) * mm});
            skLineSegment(sketch, "E32.0.6.19", {"start": v(-12, 77.4) * mm, "end": v(-10, 77.4) * mm});
            skLineSegment(sketch, "E32.0.6.20", {"start": v(-12, 71) * mm, "end": v(-12, 71.4) * mm});
            skLineSegment(sketch, "E32.0.6.21", {"start": v(-10, 74) * mm, "end": v(-10, 74.4) * mm});
            skLineSegment(sketch, "E32.0.6.22", {"start": v(-10, 77) * mm, "end": v(-10, 77.4) * mm});
            skLineSegment(sketch, "E32.0.6.23", {"start": v(-12, 79) * mm, "end": v(-12, 79.4) * mm});
            skLineSegment(sketch, "E32.0.6.24", {"start": v(-10, 75) * mm, "end": v(-10, 75.4) * mm});
            skLineSegment(sketch, "E32.0.6.25", {"start": v(-12, 74) * mm, "end": v(-12, 74.4) * mm});
            skLineSegment(sketch, "E32.0.6.26", {"start": v(-12, 76) * mm, "end": v(-12, 76.4) * mm});
            skLineSegment(sketch, "E32.0.6.27", {"start": v(-10, 78) * mm, "end": v(-10, 78.4) * mm});
            skLineSegment(sketch, "E32.0.6.28", {"start": v(-12, 78) * mm, "end": v(-12, 78.4) * mm});
            skLineSegment(sketch, "E32.0.6.29", {"start": v(-10, 71) * mm, "end": v(-10, 71.4) * mm});
            skLineSegment(sketch, "E32.0.6.30", {"start": v(-10, 76) * mm, "end": v(-10, 76.4) * mm});
            skLineSegment(sketch, "E32.0.6.31", {"start": v(-10, 79) * mm, "end": v(-10, 79.4) * mm});
            skLineSegment(sketch, "E32.0.6.32", {"start": v(-12, 72) * mm, "end": v(-12, 72.4) * mm});
            skLineSegment(sketch, "E32.0.6.33", {"start": v(-10, 73) * mm, "end": v(-10, 73.4) * mm});
            skLineSegment(sketch, "E32.0.6.34", {"start": v(-13, 75) * mm, "end": v(-13, 75.4) * mm});
            skLineSegment(sketch, "E32.0.6.35", {"start": v(-10, 72) * mm, "end": v(-10, 72.4) * mm});
            skLineSegment(sketch, "E32.0.6.36", {"start": v(-12, 77) * mm, "end": v(-12, 77.4) * mm});
            skLineSegment(sketch, "E32.0.6.37", {"start": v(-12, 73) * mm, "end": v(-12, 73.4) * mm});
            skLineSegment(sketch, "E32.0.7.0", {"start": v(-12, 82) * mm, "end": v(-10, 82) * mm});
            skLineSegment(sketch, "E32.0.7.1", {"start": v(-12, 81.4) * mm, "end": v(-10, 81.4) * mm});
            skLineSegment(sketch, "E32.0.7.2", {"start": v(-12, 83.4) * mm, "end": v(-10, 83.4) * mm});
            skLineSegment(sketch, "E32.0.7.3", {"start": v(-12, 88.4) * mm, "end": v(-10, 88.4) * mm});
            skLineSegment(sketch, "E32.0.7.4", {"start": v(-12, 82.4) * mm, "end": v(-10, 82.4) * mm});
            skLineSegment(sketch, "E32.0.7.5", {"start": v(-12, 83) * mm, "end": v(-10, 83) * mm});
            skLineSegment(sketch, "E32.0.7.6", {"start": v(-10, 85.4) * mm, "end": v(-13, 85.4) * mm});
            skLineSegment(sketch, "E32.0.7.7", {"start": v(-12, 89) * mm, "end": v(-10, 89) * mm});
            skLineSegment(sketch, "E32.0.7.8", {"start": v(-12, 89.4) * mm, "end": v(-10, 89.4) * mm});
            skLineSegment(sketch, "E32.0.7.9", {"start": v(-12, 84.4) * mm, "end": v(-10, 84.4) * mm});
            skLineSegment(sketch, "E32.0.7.10", {"start": v(-12, 88) * mm, "end": v(-10, 88) * mm});
            skLineSegment(sketch, "E32.0.7.11", {"start": v(-12, 86) * mm, "end": v(-10, 86) * mm});
            skLineSegment(sketch, "E32.0.7.12", {"start": v(-12, 87) * mm, "end": v(-10, 87) * mm});
            skLineSegment(sketch, "E32.0.7.13", {"start": v(-12, 86.4) * mm, "end": v(-10, 86.4) * mm});
            skLineSegment(sketch, "E32.0.7.14", {"start": v(-12, 81) * mm, "end": v(-10, 81) * mm});
            skLineSegment(sketch, "E32.0.7.15", {"start": v(-10, 85) * mm, "end": v(-13, 85) * mm});
            skLineSegment(sketch, "E32.0.7.16", {"start": v(-12, 70) * mm, "end": v(-12, 220) * mm, "construction": true});
            skLineSegment(sketch, "E32.0.7.17", {"start": v(-13, 70) * mm, "end": v(-13, 220) * mm, "construction": true});
            skLineSegment(sketch, "E32.0.7.18", {"start": v(-12, 84) * mm, "end": v(-10, 84) * mm});
            skLineSegment(sketch, "E32.0.7.19", {"start": v(-12, 87.4) * mm, "end": v(-10, 87.4) * mm});
            skLineSegment(sketch, "E32.0.7.20", {"start": v(-12, 81) * mm, "end": v(-12, 81.4) * mm});
            skLineSegment(sketch, "E32.0.7.21", {"start": v(-10, 84) * mm, "end": v(-10, 84.4) * mm});
            skLineSegment(sketch, "E32.0.7.22", {"start": v(-10, 87) * mm, "end": v(-10, 87.4) * mm});
            skLineSegment(sketch, "E32.0.7.23", {"start": v(-12, 89) * mm, "end": v(-12, 89.4) * mm});
            skLineSegment(sketch, "E32.0.7.24", {"start": v(-10, 85) * mm, "end": v(-10, 85.4) * mm});
            skLineSegment(sketch, "E32.0.7.25", {"start": v(-12, 84) * mm, "end": v(-12, 84.4) * mm});
            skLineSegment(sketch, "E32.0.7.26", {"start": v(-12, 86) * mm, "end": v(-12, 86.4) * mm});
            skLineSegment(sketch, "E32.0.7.27", {"start": v(-10, 88) * mm, "end": v(-10, 88.4) * mm});
            skLineSegment(sketch, "E32.0.7.28", {"start": v(-12, 88) * mm, "end": v(-12, 88.4) * mm});
            skLineSegment(sketch, "E32.0.7.29", {"start": v(-10, 81) * mm, "end": v(-10, 81.4) * mm});
            skLineSegment(sketch, "E32.0.7.30", {"start": v(-10, 86) * mm, "end": v(-10, 86.4) * mm});
            skLineSegment(sketch, "E32.0.7.31", {"start": v(-10, 89) * mm, "end": v(-10, 89.4) * mm});
            skLineSegment(sketch, "E32.0.7.32", {"start": v(-12, 82) * mm, "end": v(-12, 82.4) * mm});
            skLineSegment(sketch, "E32.0.7.33", {"start": v(-10, 83) * mm, "end": v(-10, 83.4) * mm});
            skLineSegment(sketch, "E32.0.7.34", {"start": v(-13, 85) * mm, "end": v(-13, 85.4) * mm});
            skLineSegment(sketch, "E32.0.7.35", {"start": v(-10, 82) * mm, "end": v(-10, 82.4) * mm});
            skLineSegment(sketch, "E32.0.7.36", {"start": v(-12, 87) * mm, "end": v(-12, 87.4) * mm});
            skLineSegment(sketch, "E32.0.7.37", {"start": v(-12, 83) * mm, "end": v(-12, 83.4) * mm});
            skLineSegment(sketch, "E32.0.8.0", {"start": v(-12, 92) * mm, "end": v(-10, 92) * mm});
            skLineSegment(sketch, "E32.0.8.1", {"start": v(-12, 91.4) * mm, "end": v(-10, 91.4) * mm});
            skLineSegment(sketch, "E32.0.8.2", {"start": v(-12, 93.4) * mm, "end": v(-10, 93.4) * mm});
            skLineSegment(sketch, "E32.0.8.3", {"start": v(-12, 98.4) * mm, "end": v(-10, 98.4) * mm});
            skLineSegment(sketch, "E32.0.8.4", {"start": v(-12, 92.4) * mm, "end": v(-10, 92.4) * mm});
            skLineSegment(sketch, "E32.0.8.5", {"start": v(-12, 93) * mm, "end": v(-10, 93) * mm});
            skLineSegment(sketch, "E32.0.8.6", {"start": v(-10, 95.4) * mm, "end": v(-13, 95.4) * mm});
            skLineSegment(sketch, "E32.0.8.7", {"start": v(-12, 99) * mm, "end": v(-10, 99) * mm});
            skLineSegment(sketch, "E32.0.8.8", {"start": v(-12, 99.4) * mm, "end": v(-10, 99.4) * mm});
            skLineSegment(sketch, "E32.0.8.9", {"start": v(-12, 94.4) * mm, "end": v(-10, 94.4) * mm});
            skLineSegment(sketch, "E32.0.8.10", {"start": v(-12, 98) * mm, "end": v(-10, 98) * mm});
            skLineSegment(sketch, "E32.0.8.11", {"start": v(-12, 96) * mm, "end": v(-10, 96) * mm});
            skLineSegment(sketch, "E32.0.8.12", {"start": v(-12, 97) * mm, "end": v(-10, 97) * mm});
            skLineSegment(sketch, "E32.0.8.13", {"start": v(-12, 96.4) * mm, "end": v(-10, 96.4) * mm});
            skLineSegment(sketch, "E32.0.8.14", {"start": v(-12, 91) * mm, "end": v(-10, 91) * mm});
            skLineSegment(sketch, "E32.0.8.15", {"start": v(-10, 95) * mm, "end": v(-13, 95) * mm});
            skLineSegment(sketch, "E32.0.8.16", {"start": v(-12, 80) * mm, "end": v(-12, 230) * mm, "construction": true});
            skLineSegment(sketch, "E32.0.8.17", {"start": v(-13, 80) * mm, "end": v(-13, 230) * mm, "construction": true});
            skLineSegment(sketch, "E32.0.8.18", {"start": v(-12, 94) * mm, "end": v(-10, 94) * mm});
            skLineSegment(sketch, "E32.0.8.19", {"start": v(-12, 97.4) * mm, "end": v(-10, 97.4) * mm});
            skLineSegment(sketch, "E32.0.8.20", {"start": v(-12, 91) * mm, "end": v(-12, 91.4) * mm});
            skLineSegment(sketch, "E32.0.8.21", {"start": v(-10, 94) * mm, "end": v(-10, 94.4) * mm});
            skLineSegment(sketch, "E32.0.8.22", {"start": v(-10, 97) * mm, "end": v(-10, 97.4) * mm});
            skLineSegment(sketch, "E32.0.8.23", {"start": v(-12, 99) * mm, "end": v(-12, 99.4) * mm});
            skLineSegment(sketch, "E32.0.8.24", {"start": v(-10, 95) * mm, "end": v(-10, 95.4) * mm});
            skLineSegment(sketch, "E32.0.8.25", {"start": v(-12, 94) * mm, "end": v(-12, 94.4) * mm});
            skLineSegment(sketch, "E32.0.8.26", {"start": v(-12, 96) * mm, "end": v(-12, 96.4) * mm});
            skLineSegment(sketch, "E32.0.8.27", {"start": v(-10, 98) * mm, "end": v(-10, 98.4) * mm});
            skLineSegment(sketch, "E32.0.8.28", {"start": v(-12, 98) * mm, "end": v(-12, 98.4) * mm});
            skLineSegment(sketch, "E32.0.8.29", {"start": v(-10, 91) * mm, "end": v(-10, 91.4) * mm});
            skLineSegment(sketch, "E32.0.8.30", {"start": v(-10, 96) * mm, "end": v(-10, 96.4) * mm});
            skLineSegment(sketch, "E32.0.8.31", {"start": v(-10, 99) * mm, "end": v(-10, 99.4) * mm});
            skLineSegment(sketch, "E32.0.8.32", {"start": v(-12, 92) * mm, "end": v(-12, 92.4) * mm});
            skLineSegment(sketch, "E32.0.8.33", {"start": v(-10, 93) * mm, "end": v(-10, 93.4) * mm});
            skLineSegment(sketch, "E32.0.8.34", {"start": v(-13, 95) * mm, "end": v(-13, 95.4) * mm});
            skLineSegment(sketch, "E32.0.8.35", {"start": v(-10, 92) * mm, "end": v(-10, 92.4) * mm});
            skLineSegment(sketch, "E32.0.8.36", {"start": v(-12, 97) * mm, "end": v(-12, 97.4) * mm});
            skLineSegment(sketch, "E32.0.8.37", {"start": v(-12, 93) * mm, "end": v(-12, 93.4) * mm});
            skLineSegment(sketch, "E32.0.9.0", {"start": v(-12, 102) * mm, "end": v(-10, 102) * mm});
            skLineSegment(sketch, "E32.0.9.1", {"start": v(-12, 101.4) * mm, "end": v(-10, 101.4) * mm});
            skLineSegment(sketch, "E32.0.9.2", {"start": v(-12, 103.4) * mm, "end": v(-10, 103.4) * mm});
            skLineSegment(sketch, "E32.0.9.3", {"start": v(-12, 108.4) * mm, "end": v(-10, 108.4) * mm});
            skLineSegment(sketch, "E32.0.9.4", {"start": v(-12, 102.4) * mm, "end": v(-10, 102.4) * mm});
            skLineSegment(sketch, "E32.0.9.5", {"start": v(-12, 103) * mm, "end": v(-10, 103) * mm});
            skLineSegment(sketch, "E32.0.9.6", {"start": v(-10, 105.4) * mm, "end": v(-13, 105.4) * mm});
            skLineSegment(sketch, "E32.0.9.7", {"start": v(-12, 109) * mm, "end": v(-10, 109) * mm});
            skLineSegment(sketch, "E32.0.9.8", {"start": v(-12, 109.4) * mm, "end": v(-10, 109.4) * mm});
            skLineSegment(sketch, "E32.0.9.9", {"start": v(-12, 104.4) * mm, "end": v(-10, 104.4) * mm});
            skLineSegment(sketch, "E32.0.9.10", {"start": v(-12, 108) * mm, "end": v(-10, 108) * mm});
            skLineSegment(sketch, "E32.0.9.11", {"start": v(-12, 106) * mm, "end": v(-10, 106) * mm});
            skLineSegment(sketch, "E32.0.9.12", {"start": v(-12, 107) * mm, "end": v(-10, 107) * mm});
            skLineSegment(sketch, "E32.0.9.13", {"start": v(-12, 106.4) * mm, "end": v(-10, 106.4) * mm});
            skLineSegment(sketch, "E32.0.9.14", {"start": v(-12, 101) * mm, "end": v(-10, 101) * mm});
            skLineSegment(sketch, "E32.0.9.15", {"start": v(-10, 105) * mm, "end": v(-13, 105) * mm});
            skLineSegment(sketch, "E32.0.9.16", {"start": v(-12, 90) * mm, "end": v(-12, 240) * mm, "construction": true});
            skLineSegment(sketch, "E32.0.9.17", {"start": v(-13, 90) * mm, "end": v(-13, 240) * mm, "construction": true});
            skLineSegment(sketch, "E32.0.9.18", {"start": v(-12, 104) * mm, "end": v(-10, 104) * mm});
            skLineSegment(sketch, "E32.0.9.19", {"start": v(-12, 107.4) * mm, "end": v(-10, 107.4) * mm});
            skLineSegment(sketch, "E32.0.9.20", {"start": v(-12, 101) * mm, "end": v(-12, 101.4) * mm});
            skLineSegment(sketch, "E32.0.9.21", {"start": v(-10, 104) * mm, "end": v(-10, 104.4) * mm});
            skLineSegment(sketch, "E32.0.9.22", {"start": v(-10, 107) * mm, "end": v(-10, 107.4) * mm});
            skLineSegment(sketch, "E32.0.9.23", {"start": v(-12, 109) * mm, "end": v(-12, 109.4) * mm});
            skLineSegment(sketch, "E32.0.9.24", {"start": v(-10, 105) * mm, "end": v(-10, 105.4) * mm});
            skLineSegment(sketch, "E32.0.9.25", {"start": v(-12, 104) * mm, "end": v(-12, 104.4) * mm});
            skLineSegment(sketch, "E32.0.9.26", {"start": v(-12, 106) * mm, "end": v(-12, 106.4) * mm});
            skLineSegment(sketch, "E32.0.9.27", {"start": v(-10, 108) * mm, "end": v(-10, 108.4) * mm});
            skLineSegment(sketch, "E32.0.9.28", {"start": v(-12, 108) * mm, "end": v(-12, 108.4) * mm});
            skLineSegment(sketch, "E32.0.9.29", {"start": v(-10, 101) * mm, "end": v(-10, 101.4) * mm});
            skLineSegment(sketch, "E32.0.9.30", {"start": v(-10, 106) * mm, "end": v(-10, 106.4) * mm});
            skLineSegment(sketch, "E32.0.9.31", {"start": v(-10, 109) * mm, "end": v(-10, 109.4) * mm});
            skLineSegment(sketch, "E32.0.9.32", {"start": v(-12, 102) * mm, "end": v(-12, 102.4) * mm});
            skLineSegment(sketch, "E32.0.9.33", {"start": v(-10, 103) * mm, "end": v(-10, 103.4) * mm});
            skLineSegment(sketch, "E32.0.9.34", {"start": v(-13, 105) * mm, "end": v(-13, 105.4) * mm});
            skLineSegment(sketch, "E32.0.9.35", {"start": v(-10, 102) * mm, "end": v(-10, 102.4) * mm});
            skLineSegment(sketch, "E32.0.9.36", {"start": v(-12, 107) * mm, "end": v(-12, 107.4) * mm});
            skLineSegment(sketch, "E32.0.9.37", {"start": v(-12, 103) * mm, "end": v(-12, 103.4) * mm});
            skLineSegment(sketch, "E32.0.10.0", {"start": v(-12, 112) * mm, "end": v(-10, 112) * mm});
            skLineSegment(sketch, "E32.0.10.1", {"start": v(-12, 111.4) * mm, "end": v(-10, 111.4) * mm});
            skLineSegment(sketch, "E32.0.10.2", {"start": v(-12, 113.4) * mm, "end": v(-10, 113.4) * mm});
            skLineSegment(sketch, "E32.0.10.3", {"start": v(-12, 118.4) * mm, "end": v(-10, 118.4) * mm});
            skLineSegment(sketch, "E32.0.10.4", {"start": v(-12, 112.4) * mm, "end": v(-10, 112.4) * mm});
            skLineSegment(sketch, "E32.0.10.5", {"start": v(-12, 113) * mm, "end": v(-10, 113) * mm});
            skLineSegment(sketch, "E32.0.10.6", {"start": v(-10, 115.4) * mm, "end": v(-13, 115.4) * mm});
            skLineSegment(sketch, "E32.0.10.7", {"start": v(-12, 119) * mm, "end": v(-10, 119) * mm});
            skLineSegment(sketch, "E32.0.10.8", {"start": v(-12, 119.4) * mm, "end": v(-10, 119.4) * mm});
            skLineSegment(sketch, "E32.0.10.9", {"start": v(-12, 114.4) * mm, "end": v(-10, 114.4) * mm});
            skLineSegment(sketch, "E32.0.10.10", {"start": v(-12, 118) * mm, "end": v(-10, 118) * mm});
            skLineSegment(sketch, "E32.0.10.11", {"start": v(-12, 116) * mm, "end": v(-10, 116) * mm});
            skLineSegment(sketch, "E32.0.10.12", {"start": v(-12, 117) * mm, "end": v(-10, 117) * mm});
            skLineSegment(sketch, "E32.0.10.13", {"start": v(-12, 116.4) * mm, "end": v(-10, 116.4) * mm});
            skLineSegment(sketch, "E32.0.10.14", {"start": v(-12, 111) * mm, "end": v(-10, 111) * mm});
            skLineSegment(sketch, "E32.0.10.15", {"start": v(-10, 115) * mm, "end": v(-13, 115) * mm});
            skLineSegment(sketch, "E32.0.10.16", {"start": v(-12, 100) * mm, "end": v(-12, 250) * mm, "construction": true});
            skLineSegment(sketch, "E32.0.10.17", {"start": v(-13, 100) * mm, "end": v(-13, 250) * mm, "construction": true});
            skLineSegment(sketch, "E32.0.10.18", {"start": v(-12, 114) * mm, "end": v(-10, 114) * mm});
            skLineSegment(sketch, "E32.0.10.19", {"start": v(-12, 117.4) * mm, "end": v(-10, 117.4) * mm});
            skLineSegment(sketch, "E32.0.10.20", {"start": v(-12, 111) * mm, "end": v(-12, 111.4) * mm});
            skLineSegment(sketch, "E32.0.10.21", {"start": v(-10, 114) * mm, "end": v(-10, 114.4) * mm});
            skLineSegment(sketch, "E32.0.10.22", {"start": v(-10, 117) * mm, "end": v(-10, 117.4) * mm});
            skLineSegment(sketch, "E32.0.10.23", {"start": v(-12, 119) * mm, "end": v(-12, 119.4) * mm});
            skLineSegment(sketch, "E32.0.10.24", {"start": v(-10, 115) * mm, "end": v(-10, 115.4) * mm});
            skLineSegment(sketch, "E32.0.10.25", {"start": v(-12, 114) * mm, "end": v(-12, 114.4) * mm});
            skLineSegment(sketch, "E32.0.10.26", {"start": v(-12, 116) * mm, "end": v(-12, 116.4) * mm});
            skLineSegment(sketch, "E32.0.10.27", {"start": v(-10, 118) * mm, "end": v(-10, 118.4) * mm});
            skLineSegment(sketch, "E32.0.10.28", {"start": v(-12, 118) * mm, "end": v(-12, 118.4) * mm});
            skLineSegment(sketch, "E32.0.10.29", {"start": v(-10, 111) * mm, "end": v(-10, 111.4) * mm});
            skLineSegment(sketch, "E32.0.10.30", {"start": v(-10, 116) * mm, "end": v(-10, 116.4) * mm});
            skLineSegment(sketch, "E32.0.10.31", {"start": v(-10, 119) * mm, "end": v(-10, 119.4) * mm});
            skLineSegment(sketch, "E32.0.10.32", {"start": v(-12, 112) * mm, "end": v(-12, 112.4) * mm});
            skLineSegment(sketch, "E32.0.10.33", {"start": v(-10, 113) * mm, "end": v(-10, 113.4) * mm});
            skLineSegment(sketch, "E32.0.10.34", {"start": v(-13, 115) * mm, "end": v(-13, 115.4) * mm});
            skLineSegment(sketch, "E32.0.10.35", {"start": v(-10, 112) * mm, "end": v(-10, 112.4) * mm});
            skLineSegment(sketch, "E32.0.10.36", {"start": v(-12, 117) * mm, "end": v(-12, 117.4) * mm});
            skLineSegment(sketch, "E32.0.10.37", {"start": v(-12, 113) * mm, "end": v(-12, 113.4) * mm});
            skLineSegment(sketch, "E32.0.11.0", {"start": v(-12, 122) * mm, "end": v(-10, 122) * mm});
            skLineSegment(sketch, "E32.0.11.1", {"start": v(-12, 121.4) * mm, "end": v(-10, 121.4) * mm});
            skLineSegment(sketch, "E32.0.11.2", {"start": v(-12, 123.4) * mm, "end": v(-10, 123.4) * mm});
            skLineSegment(sketch, "E32.0.11.3", {"start": v(-12, 128.4) * mm, "end": v(-10, 128.4) * mm});
            skLineSegment(sketch, "E32.0.11.4", {"start": v(-12, 122.4) * mm, "end": v(-10, 122.4) * mm});
            skLineSegment(sketch, "E32.0.11.5", {"start": v(-12, 123) * mm, "end": v(-10, 123) * mm});
            skLineSegment(sketch, "E32.0.11.6", {"start": v(-10, 125.4) * mm, "end": v(-13, 125.4) * mm});
            skLineSegment(sketch, "E32.0.11.7", {"start": v(-12, 129) * mm, "end": v(-10, 129) * mm});
            skLineSegment(sketch, "E32.0.11.8", {"start": v(-12, 129.4) * mm, "end": v(-10, 129.4) * mm});
            skLineSegment(sketch, "E32.0.11.9", {"start": v(-12, 124.4) * mm, "end": v(-10, 124.4) * mm});
            skLineSegment(sketch, "E32.0.11.10", {"start": v(-12, 128) * mm, "end": v(-10, 128) * mm});
            skLineSegment(sketch, "E32.0.11.11", {"start": v(-12, 126) * mm, "end": v(-10, 126) * mm});
            skLineSegment(sketch, "E32.0.11.12", {"start": v(-12, 127) * mm, "end": v(-10, 127) * mm});
            skLineSegment(sketch, "E32.0.11.13", {"start": v(-12, 126.4) * mm, "end": v(-10, 126.4) * mm});
            skLineSegment(sketch, "E32.0.11.14", {"start": v(-12, 121) * mm, "end": v(-10, 121) * mm});
            skLineSegment(sketch, "E32.0.11.15", {"start": v(-10, 125) * mm, "end": v(-13, 125) * mm});
            skLineSegment(sketch, "E32.0.11.16", {"start": v(-12, 110) * mm, "end": v(-12, 260) * mm, "construction": true});
            skLineSegment(sketch, "E32.0.11.17", {"start": v(-13, 110) * mm, "end": v(-13, 260) * mm, "construction": true});
            skLineSegment(sketch, "E32.0.11.18", {"start": v(-12, 124) * mm, "end": v(-10, 124) * mm});
            skLineSegment(sketch, "E32.0.11.19", {"start": v(-12, 127.4) * mm, "end": v(-10, 127.4) * mm});
            skLineSegment(sketch, "E32.0.11.20", {"start": v(-12, 121) * mm, "end": v(-12, 121.4) * mm});
            skLineSegment(sketch, "E32.0.11.21", {"start": v(-10, 124) * mm, "end": v(-10, 124.4) * mm});
            skLineSegment(sketch, "E32.0.11.22", {"start": v(-10, 127) * mm, "end": v(-10, 127.4) * mm});
            skLineSegment(sketch, "E32.0.11.23", {"start": v(-12, 129) * mm, "end": v(-12, 129.4) * mm});
            skLineSegment(sketch, "E32.0.11.24", {"start": v(-10, 125) * mm, "end": v(-10, 125.4) * mm});
            skLineSegment(sketch, "E32.0.11.25", {"start": v(-12, 124) * mm, "end": v(-12, 124.4) * mm});
            skLineSegment(sketch, "E32.0.11.26", {"start": v(-12, 126) * mm, "end": v(-12, 126.4) * mm});
            skLineSegment(sketch, "E32.0.11.27", {"start": v(-10, 128) * mm, "end": v(-10, 128.4) * mm});
            skLineSegment(sketch, "E32.0.11.28", {"start": v(-12, 128) * mm, "end": v(-12, 128.4) * mm});
            skLineSegment(sketch, "E32.0.11.29", {"start": v(-10, 121) * mm, "end": v(-10, 121.4) * mm});
            skLineSegment(sketch, "E32.0.11.30", {"start": v(-10, 126) * mm, "end": v(-10, 126.4) * mm});
            skLineSegment(sketch, "E32.0.11.31", {"start": v(-10, 129) * mm, "end": v(-10, 129.4) * mm});
            skLineSegment(sketch, "E32.0.11.32", {"start": v(-12, 122) * mm, "end": v(-12, 122.4) * mm});
            skLineSegment(sketch, "E32.0.11.33", {"start": v(-10, 123) * mm, "end": v(-10, 123.4) * mm});
            skLineSegment(sketch, "E32.0.11.34", {"start": v(-13, 125) * mm, "end": v(-13, 125.4) * mm});
            skLineSegment(sketch, "E32.0.11.35", {"start": v(-10, 122) * mm, "end": v(-10, 122.4) * mm});
            skLineSegment(sketch, "E32.0.11.36", {"start": v(-12, 127) * mm, "end": v(-12, 127.4) * mm});
            skLineSegment(sketch, "E32.0.11.37", {"start": v(-12, 123) * mm, "end": v(-12, 123.4) * mm});
            skLineSegment(sketch, "E32.0.12.0", {"start": v(-12, 132) * mm, "end": v(-10, 132) * mm});
            skLineSegment(sketch, "E32.0.12.1", {"start": v(-12, 131.4) * mm, "end": v(-10, 131.4) * mm});
            skLineSegment(sketch, "E32.0.12.2", {"start": v(-12, 133.4) * mm, "end": v(-10, 133.4) * mm});
            skLineSegment(sketch, "E32.0.12.3", {"start": v(-12, 138.4) * mm, "end": v(-10, 138.4) * mm});
            skLineSegment(sketch, "E32.0.12.4", {"start": v(-12, 132.4) * mm, "end": v(-10, 132.4) * mm});
            skLineSegment(sketch, "E32.0.12.5", {"start": v(-12, 133) * mm, "end": v(-10, 133) * mm});
            skLineSegment(sketch, "E32.0.12.6", {"start": v(-10, 135.4) * mm, "end": v(-13, 135.4) * mm});
            skLineSegment(sketch, "E32.0.12.7", {"start": v(-12, 139) * mm, "end": v(-10, 139) * mm});
            skLineSegment(sketch, "E32.0.12.8", {"start": v(-12, 139.4) * mm, "end": v(-10, 139.4) * mm});
            skLineSegment(sketch, "E32.0.12.9", {"start": v(-12, 134.4) * mm, "end": v(-10, 134.4) * mm});
            skLineSegment(sketch, "E32.0.12.10", {"start": v(-12, 138) * mm, "end": v(-10, 138) * mm});
            skLineSegment(sketch, "E32.0.12.11", {"start": v(-12, 136) * mm, "end": v(-10, 136) * mm});
            skLineSegment(sketch, "E32.0.12.12", {"start": v(-12, 137) * mm, "end": v(-10, 137) * mm});
            skLineSegment(sketch, "E32.0.12.13", {"start": v(-12, 136.4) * mm, "end": v(-10, 136.4) * mm});
            skLineSegment(sketch, "E32.0.12.14", {"start": v(-12, 131) * mm, "end": v(-10, 131) * mm});
            skLineSegment(sketch, "E32.0.12.15", {"start": v(-10, 135) * mm, "end": v(-13, 135) * mm});
            skLineSegment(sketch, "E32.0.12.16", {"start": v(-12, 120) * mm, "end": v(-12, 270) * mm, "construction": true});
            skLineSegment(sketch, "E32.0.12.17", {"start": v(-13, 120) * mm, "end": v(-13, 270) * mm, "construction": true});
            skLineSegment(sketch, "E32.0.12.18", {"start": v(-12, 134) * mm, "end": v(-10, 134) * mm});
            skLineSegment(sketch, "E32.0.12.19", {"start": v(-12, 137.4) * mm, "end": v(-10, 137.4) * mm});
            skLineSegment(sketch, "E32.0.12.20", {"start": v(-12, 131) * mm, "end": v(-12, 131.4) * mm});
            skLineSegment(sketch, "E32.0.12.21", {"start": v(-10, 134) * mm, "end": v(-10, 134.4) * mm});
            skLineSegment(sketch, "E32.0.12.22", {"start": v(-10, 137) * mm, "end": v(-10, 137.4) * mm});
            skLineSegment(sketch, "E32.0.12.23", {"start": v(-12, 139) * mm, "end": v(-12, 139.4) * mm});
            skLineSegment(sketch, "E32.0.12.24", {"start": v(-10, 135) * mm, "end": v(-10, 135.4) * mm});
            skLineSegment(sketch, "E32.0.12.25", {"start": v(-12, 134) * mm, "end": v(-12, 134.4) * mm});
            skLineSegment(sketch, "E32.0.12.26", {"start": v(-12, 136) * mm, "end": v(-12, 136.4) * mm});
            skLineSegment(sketch, "E32.0.12.27", {"start": v(-10, 138) * mm, "end": v(-10, 138.4) * mm});
            skLineSegment(sketch, "E32.0.12.28", {"start": v(-12, 138) * mm, "end": v(-12, 138.4) * mm});
            skLineSegment(sketch, "E32.0.12.29", {"start": v(-10, 131) * mm, "end": v(-10, 131.4) * mm});
            skLineSegment(sketch, "E32.0.12.30", {"start": v(-10, 136) * mm, "end": v(-10, 136.4) * mm});
            skLineSegment(sketch, "E32.0.12.31", {"start": v(-10, 139) * mm, "end": v(-10, 139.4) * mm});
            skLineSegment(sketch, "E32.0.12.32", {"start": v(-12, 132) * mm, "end": v(-12, 132.4) * mm});
            skLineSegment(sketch, "E32.0.12.33", {"start": v(-10, 133) * mm, "end": v(-10, 133.4) * mm});
            skLineSegment(sketch, "E32.0.12.34", {"start": v(-13, 135) * mm, "end": v(-13, 135.4) * mm});
            skLineSegment(sketch, "E32.0.12.35", {"start": v(-10, 132) * mm, "end": v(-10, 132.4) * mm});
            skLineSegment(sketch, "E32.0.12.36", {"start": v(-12, 137) * mm, "end": v(-12, 137.4) * mm});
            skLineSegment(sketch, "E32.0.12.37", {"start": v(-12, 133) * mm, "end": v(-12, 133.4) * mm});
            skLineSegment(sketch, "E32.direction1", {"start": v(-13, 0) * mm, "end": v(12, 0) * mm, "construction": true});
            skLineSegment(sketch, "E32.direction2", {"start": v(-13, 0) * mm, "end": v(-13, 10) * mm, "construction": true});
            const initialGuessF2  = {"E10": [-0.017, 0.01082, 0, -1, 0.002], "E11": [-0.015, 0.01943, 0, 1, 0.002], "E12": [-0.015, 0.0292, 0, 1, 0.002], "E13": [-0.015, 0.0392, 0, 1, 0.002], "E14": [-0.015, 0.04914, 0, 1, 0.002], "E15": [-0.015, 0.0592, 0, 1, 0.002], "E16": [-0.015, 0.069, 0, 1, 0.00247], "E17": [-0.015, 0.079, 0, 1, 0.00247], "E18": [-0.015, 0.089, 0, 1, 0.00247], "E19": [-0.015, 0.099, 0, 1, 0.00247], "E20": [-0.015, 0.10821, 0, 1, 0.00222], "E21": [-0.015, 0.11848, 0, 1, 0.00222], "E22": [-0.015, 0.12822, 0, 1, 0.00222], "E23": [-0.015, 0.13823, 0, 1, 0.00222]};
            skSetInitialGuess(sketch, initialGuessF2);
            skSolve(sketch);
        }
        {
            var Q0;
            Q0=qSketchRegion(id+"F2",true);
            extrude(context, id + "F3", {"entities" : qUnion([Q0]), "operationType" : NewBodyOperationType.ADD, "endBound" : BoundingType.SYMMETRIC, "oppositeDirection" : true, "depth" : 10 * mm, "offsetDistance" : 25 * mm});
        }
    });
